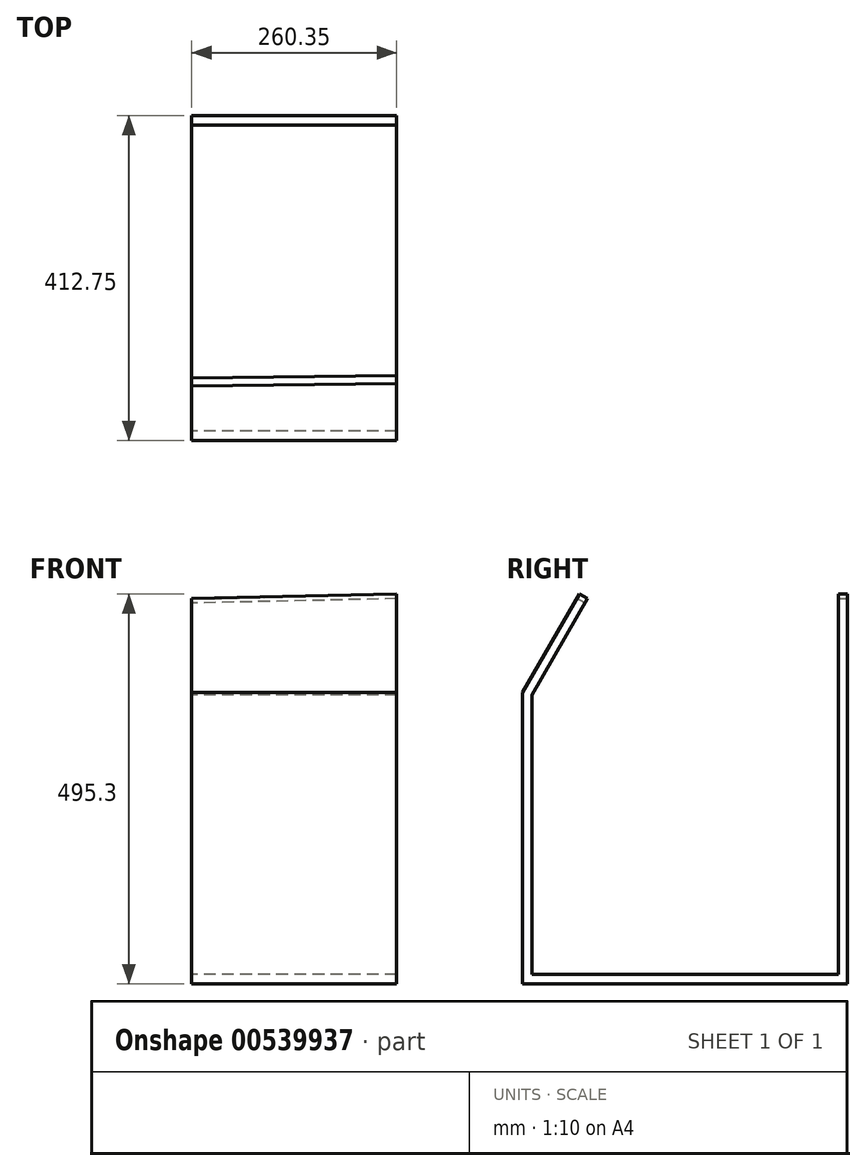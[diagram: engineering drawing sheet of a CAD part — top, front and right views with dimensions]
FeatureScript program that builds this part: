
annotation { "Feature Type Name" : "Feature", "Feature Type Description" : "" }
export const myFeature = defineFeature(function(context is Context, id is Id, definition is map)
    precondition{}
    {
        {
            var Q0;
            Q0=qCreatedBy(makeId("Right.planeOp"),FACE);
            var sketch = newSketch(context, id + "F0", { "sketchPlane" : qUnion([Q0])});
            skLineSegment(sketch, "E0", {"start": v(0, 0) * mm, "end": v(0, -483.4) * mm});
            skLineSegment(sketch, "E1", {"start": v(0, -483.4) * mm, "end": v(-388.94, -483.4) * mm});
            skLineSegment(sketch, "E2", {"start": v(-388.94, -483.4) * mm, "end": v(-388.94, -128.3) * mm});
            skLineSegment(sketch, "E3", {"start": v(-388.94, -128.3) * mm, "end": v(-318.3, -5.95) * mm});
            skLineSegment(sketch, "E4.0", {"start": v(-400.84, -125.1) * mm, "end": v(-328.61, 0) * mm});
            skLineSegment(sketch, "E4.1", {"start": v(-400.84, -495.3) * mm, "end": v(-400.84, -125.1) * mm});
            skLineSegment(sketch, "E4.2", {"start": v(11.9, -495.3) * mm, "end": v(-400.84, -495.3) * mm});
            skLineSegment(sketch, "E4.3", {"start": v(11.9, 0) * mm, "end": v(11.9, -495.3) * mm});
            skLineSegment(sketch, "E5", {"start": v(-328.61, 0) * mm, "end": v(-318.3, -5.95) * mm});
            skLineSegment(sketch, "E6", {"start": v(0, 0) * mm, "end": v(11.9, 0) * mm});
            skSolve(sketch);
        }
        {
            var Q0;
            Q0 = qSketchRegion(id + "F0", true);
            extrude(context, id + "F1", {"entities" : qUnion([Q0]), "depth" : 260.35 * mm, "offsetDistance" : 25.4 * mm});
        }
        {
            var Q0;
            Q0=qCreatedBy(makeId("Front.planeOp"),FACE);
            var sketch = newSketch(context, id + "F2", { "sketchPlane" : qUnion([Q0])});
            skLineSegment(sketch, "E7", {"start": v(0, 0) * mm, "end": v(260.35, 0) * mm});
            skLineSegment(sketch, "E8", {"start": v(260.35, 0) * mm, "end": v(0, -6.35) * mm});
            skLineSegment(sketch, "E9", {"start": v(0, -6.35) * mm, "end": v(0, 0) * mm});
            skSolve(sketch);
        }
        {
            var Q0;
            Q0 = qSketchRegion(id + "F2", true);
            extrude(context, id + "F3", {"entities" : qUnion([Q0]), "operationType" : NewBodyOperationType.REMOVE, "endBound" : BoundingType.THROUGH_ALL, "oppositeDirection" : true, "depth" : 25.4 * mm, "offsetDistance" : 25.4 * mm});
        }
        {
            var Q0;
            Q0=makeQuery(id+"F1.opExtrude","SWEPT_FACE",FACE,{"disambiguationData":[OSD([sQuery(id+"F0.wireOp",EDGE,"E4.0")])]});
            var sketch = newSketch(context, id + "F4", { "sketchPlane" : qUnion([Q0])});
            skLineSegment(sketch, "E10", {"start": v(0, -164.3) * mm, "end": v(260.35, -164.3) * mm});
            skLineSegment(sketch, "E11", {"start": v(260.35, -164.3) * mm, "end": v(0, -170.66) * mm});
            skLineSegment(sketch, "E12", {"start": v(0, -170.66) * mm, "end": v(0, -164.3) * mm});
            skSolve(sketch);
        }
        {
            var Q0;
            Q0 = qSketchRegion(id + "F4", true);
            extrude(context, id + "F5", {"entities" : qUnion([Q0]), "operationType" : NewBodyOperationType.REMOVE, "oppositeDirection" : true, "depth" : 25.4 * mm, "offsetDistance" : 25.4 * mm});
        }
    });
